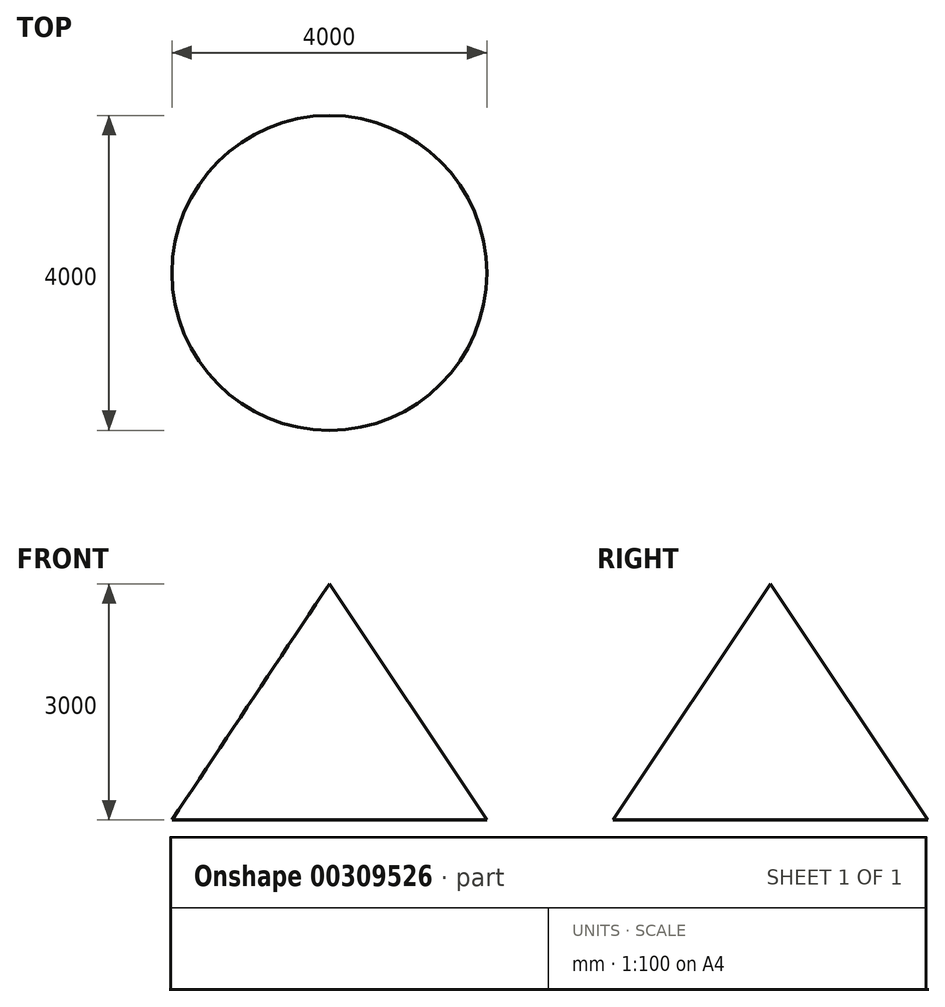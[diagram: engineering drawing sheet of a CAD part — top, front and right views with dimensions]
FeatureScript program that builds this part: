
annotation { "Feature Type Name" : "Feature", "Feature Type Description" : "" }
export const myFeature = defineFeature(function(context is Context, id is Id, definition is map)
    precondition{}
    {
        {
            var Q0;
            Q0=qCreatedBy(makeId("Front.planeOp"),FACE);
            var sketch = newSketch(context, id + "F0", { "sketchPlane" : qUnion([Q0])});
            skLineSegment(sketch, "E0", {"start": v(-2000, 0) * mm, "end": v(0, 0) * mm});
            skLineSegment(sketch, "E1", {"start": v(0, 0) * mm, "end": v(0, 3000) * mm});
            skLineSegment(sketch, "E2", {"start": v(0, 3000) * mm, "end": v(-2000, 0) * mm});
            skSolve(sketch);
        }
        {
            var Q0;
            Q0=makeQuery(id+"F0.imprint","IMPRINT",FACE,{"disambiguationData":[TD([[makeQuery(id+"F0.imprint","IMPRINT",EDGE,{"derivedFrom":sQuery(id+"F0.wireOp",EDGE,"E0")}),1.0]])]});
            var Q1;
            Q1=sQuery(id+"F0.wireOp",EDGE,"E1");
            revolve(context, id + "F1", {"entities" : qUnion([Q0]), "axis" : qUnion([Q1]), "revolveType" : RevolveType.FULL});
        }
    });
